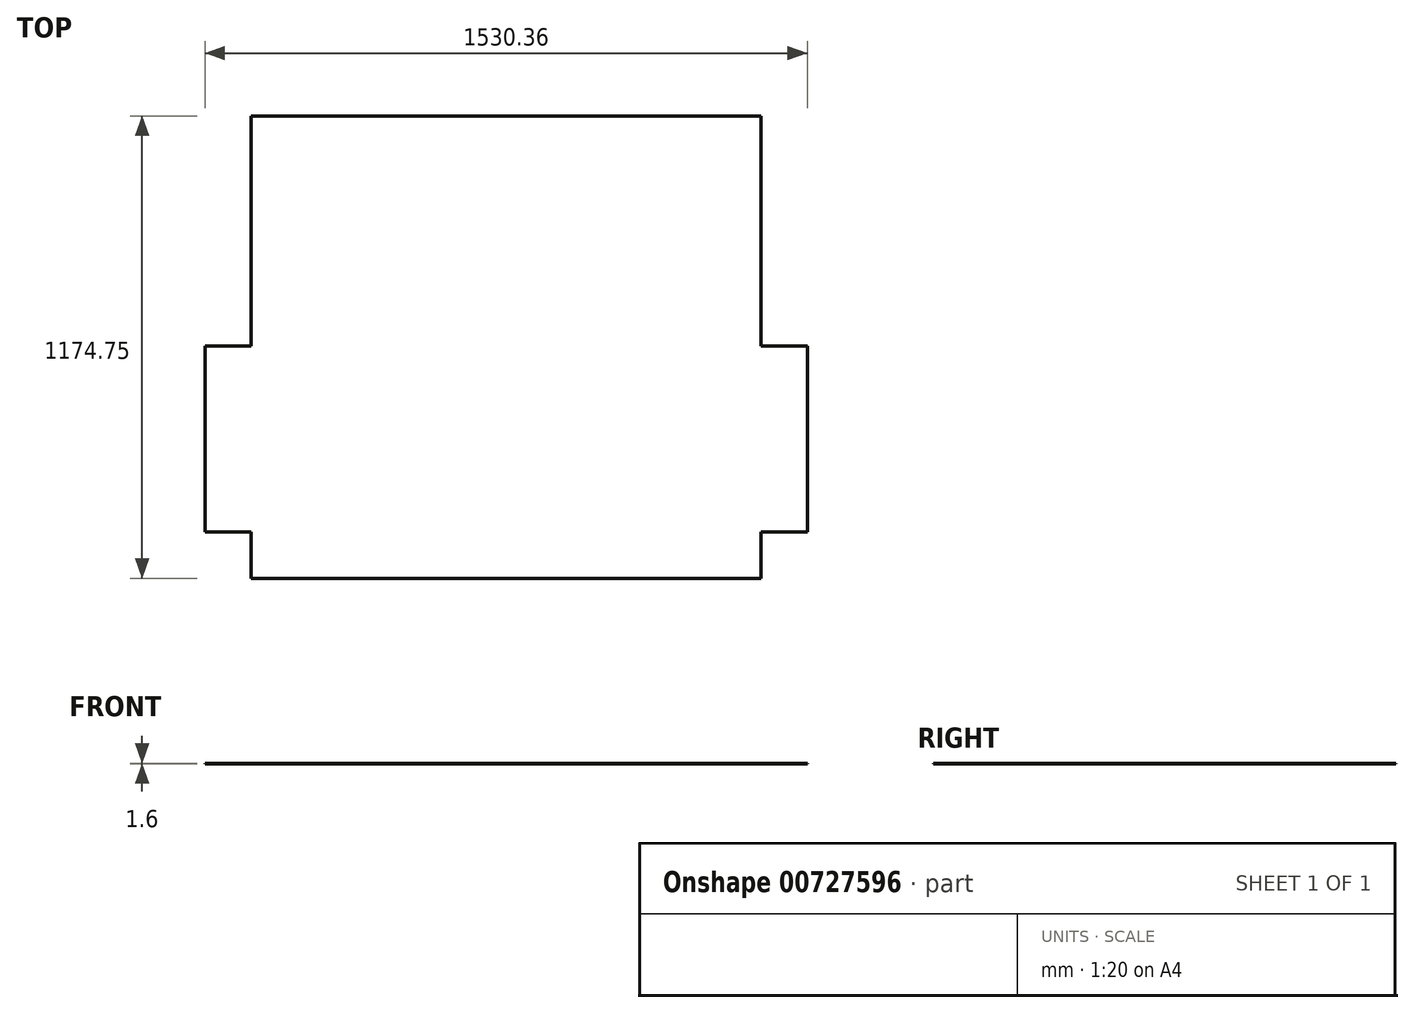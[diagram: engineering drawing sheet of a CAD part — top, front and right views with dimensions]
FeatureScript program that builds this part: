
annotation { "Feature Type Name" : "Feature", "Feature Type Description" : "" }
export const myFeature = defineFeature(function(context is Context, id is Id, definition is map)
    precondition{}
    {
        {
            var Q0;
            Q0=qCreatedBy(makeId("Top.planeOp"),FACE);
            var sketch = newSketch(context, id + "F0", { "sketchPlane" : qUnion([Q0])});
            skLineSegment(sketch, "E0.bottom", {"start": v(765.18, 236.54) * mm, "end": v(647.7, 236.54) * mm});
            skLineSegment(sketch, "E0.top", {"start": v(765.18, -236.54) * mm, "end": v(647.7, -236.54) * mm});
            skLineSegment(sketch, "E0.left", {"start": v(765.18, 236.54) * mm, "end": v(765.18, -236.54) * mm});
            skLineSegment(sketch, "E0.right", {"start": v(-765.18, 236.54) * mm, "end": v(-765.18, -236.54) * mm});
            skPoint(sketch, "E0.middle", {"position": v(0, 0) * mm});
            skLineSegment(sketch, "E1.top", {"start": v(-647.7, -354.01) * mm, "end": v(647.7, -354.01) * mm});
            skLineSegment(sketch, "E1.left", {"start": v(-647.7, -236.54) * mm, "end": v(-647.7, -354.01) * mm});
            skLineSegment(sketch, "E1.right", {"start": v(647.7, -236.54) * mm, "end": v(647.7, -354.01) * mm});
            skLineSegment(sketch, "E2.top", {"start": v(-647.7, 820.74) * mm, "end": v(647.7, 820.74) * mm});
            skLineSegment(sketch, "E2.left", {"start": v(-647.7, 236.54) * mm, "end": v(-647.7, 820.74) * mm});
            skLineSegment(sketch, "E2.right", {"start": v(647.7, 236.54) * mm, "end": v(647.7, 820.74) * mm});
            skLineSegment(sketch, "E3.trimOffspring", {"start": v(-647.7, 236.54) * mm, "end": v(-765.18, 236.54) * mm});
            skLineSegment(sketch, "E4.trimOffspring", {"start": v(-647.7, -236.54) * mm, "end": v(-765.18, -236.54) * mm});
            skSolve(sketch);
        }
        {
            var Q0;
            Q0 = qSketchRegion(id + "F0", true);
            extrude(context, id + "F1", {"entities" : qUnion([Q0]), "depth" : 1.6 * mm, "offsetDistance" : 25.4 * mm});
        }
    });
